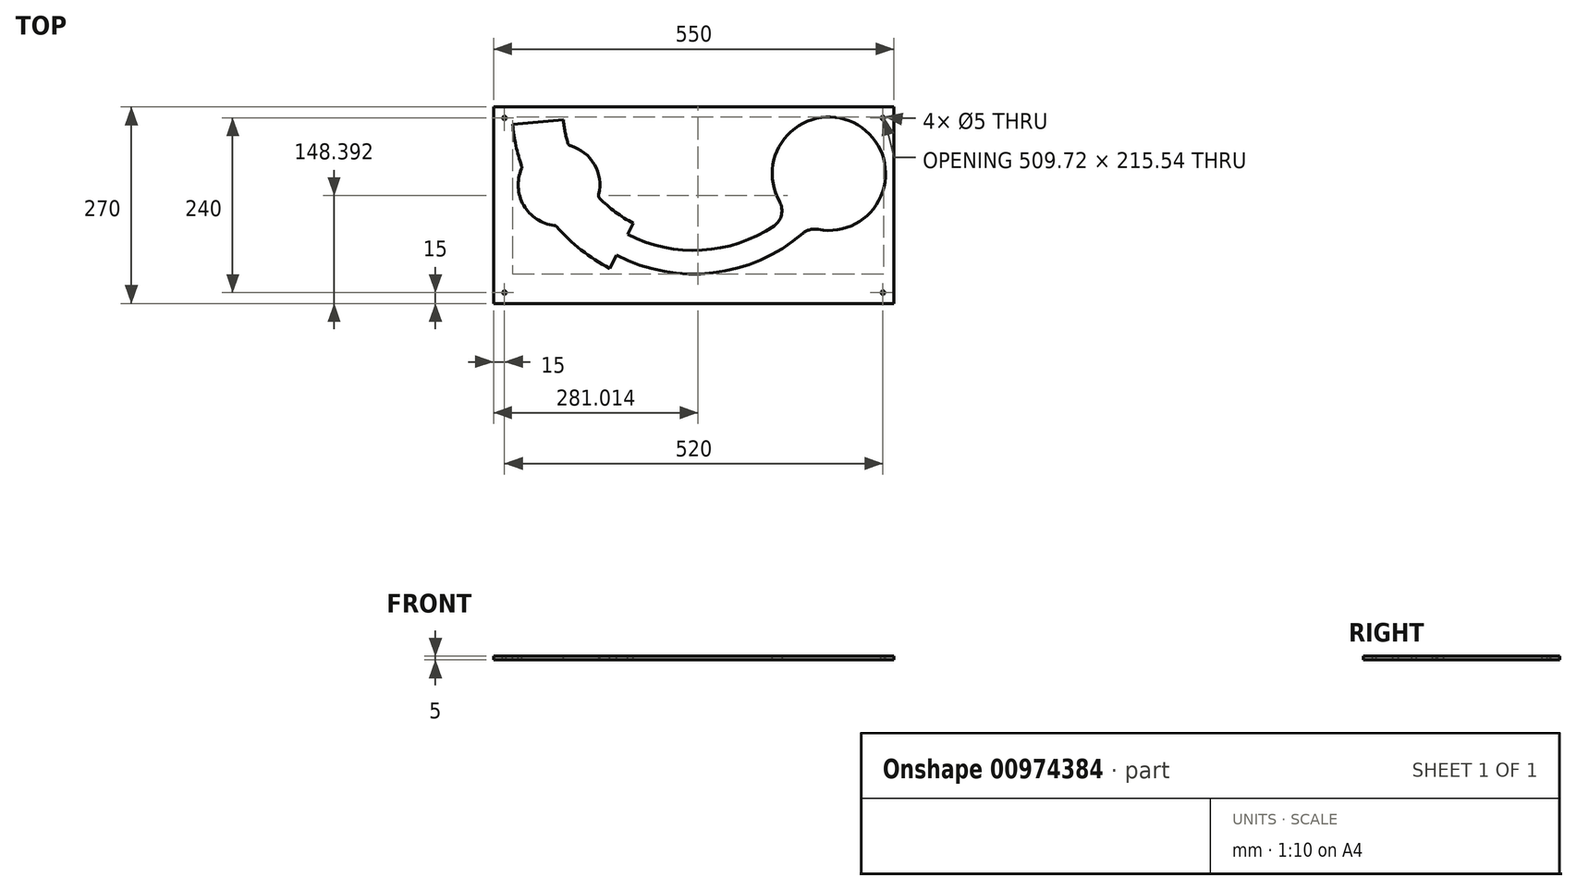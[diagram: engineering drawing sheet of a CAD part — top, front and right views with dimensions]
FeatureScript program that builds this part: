
annotation { "Feature Type Name" : "Feature", "Feature Type Description" : "" }
export const myFeature = defineFeature(function(context is Context, id is Id, definition is map)
    precondition{}
    {
        {
            var Q0;
            Q0=qCreatedBy(makeId("Top.planeOp"),FACE);
            var sketch = newSketch(context, id + "F0", { "sketchPlane" : qUnion([Q0])});
            skLineSegment(sketch, "E0.bottom", {"start": v(0, 0) * mm, "end": v(550, 0) * mm});
            skLineSegment(sketch, "E0.top", {"start": v(0, -270) * mm, "end": v(550, -270) * mm});
            skLineSegment(sketch, "E0.left", {"start": v(0, 0) * mm, "end": v(0, -270) * mm});
            skLineSegment(sketch, "E0.right", {"start": v(550, 0) * mm, "end": v(550, -270) * mm});
            skSolve(sketch);
        }
        {
            var Q0;
            Q0=makeQuery(id+"F0.imprint","IMPRINT",FACE,{"disambiguationData":[TD([[makeQuery(id+"F0.imprint","IMPRINT",EDGE,{"derivedFrom":sQuery(id+"F0.wireOp",EDGE,"E0.bottom")}),-1.0]])]});
            extrude(context, id + "F1", {"entities" : qUnion([Q0]), "oppositeDirection" : true, "depth" : 5 * mm, "offsetDistance" : 25 * mm});
        }
        {
            var Q0;
            Q0=makeQuery(id+"F1.opExtrude","CAP_FACE",FACE,{"disambiguationData":[OSD([sQuery(id+"F0.wireOp",EDGE,"E0.bottom"),sQuery(id+"F0.wireOp",EDGE,"E0.top"),sQuery(id+"F0.wireOp",EDGE,"E0.left"),sQuery(id+"F0.wireOp",EDGE,"E0.right")])],"isStart":true});
            var sketch = newSketch(context, id + "F2", { "sketchPlane" : qUnion([Q0])});
            skArc(sketch, "E1", {"start": v(26.15, -24) * mm, "mid": v(195.26, -236.94) * mm, "end": v(458.7, -169.57) * mm});
            skArc(sketch, "E2", {"start": v(95.83, -17.28) * mm, "mid": v(209.67, -167.73) * mm, "end": v(395.28, -133.91) * mm});
            skPoint(sketch, "E3.start.orphan", {"position": v(275, -180) * mm});
            skCircle(sketch, "E4", {"center": v(460.77, -91.66) * mm, "radius": 77.94 * mm});
            skLineSegment(sketch, "E5", {"start": v(95.83, -17.28) * mm, "end": v(26.15, -24) * mm});
            skLineSegment(sketch, "E6", {"start": v(191.91, -159.67) * mm, "end": v(159.6, -221.77) * mm});
            skLineSegment(sketch, "E7", {"start": v(550, 0) * mm, "end": v(535, 0) * mm});
            skLineSegment(sketch, "E8", {"start": v(535, 0) * mm, "end": v(535, -15) * mm});
            skLineSegment(sketch, "E9", {"start": v(0, -270) * mm, "end": v(15, -270) * mm});
            skLineSegment(sketch, "E10", {"start": v(15, -270) * mm, "end": v(15, -255) * mm});
            skCircle(sketch, "E11", {"center": v(15, -255) * mm, "radius": 2.5 * mm});
            skCircle(sketch, "E12", {"center": v(535, -255) * mm, "radius": 2.5 * mm});
            skCircle(sketch, "E13", {"center": v(535, -15) * mm, "radius": 2.5 * mm});
            skCircle(sketch, "E14", {"center": v(15, -15) * mm, "radius": 2.5 * mm});
            skCircle(sketch, "E15", {"center": v(89.9, -107.02) * mm, "radius": 56.06 * mm});
            skCircle(sketch, "E16", {"center": v(275, 0) * mm, "radius": 182 * mm});
            skCircle(sketch, "E17", {"center": v(275, 0) * mm, "radius": 239.5 * mm});
            skCircle(sketch, "E18", {"center": v(275, 0) * mm, "radius": 197 * mm});
            skCircle(sketch, "E19", {"center": v(275, 0) * mm, "radius": 229.5 * mm});
            skSolve(sketch);
        }
        {
            var Q0;
            {var subQ0=sQuery(id+"F2.wireOp",EDGE,"E4");var subQ1=makeQuery(id+"F2.imprint","INTERSECT",VERTEX,{"derivedFrom":[sQuery(id+"F2.wireOp",EDGE,"E1"),subQ0]});Q0=makeQuery(id+"F2.imprint","IMPRINT",FACE,{"disambiguationData":[TD([[makeQuery(id+"F2.imprint","IMPRINT",EDGE,{"disambiguationData":[TD([[subQ1,1.0]])],"derivedFrom":subQ0}),1.0]])]});}
            var Q1;
            {var subQ0=sQuery(id+"F2.wireOp",EDGE,"E19");var subQ1=sQuery(id+"F2.wireOp",EDGE,"E4");var subQ2=makeQuery(id+"F2.imprint","INTERSECT",VERTEX,{"disambiguationData":[OD(0.0)],"derivedFrom":[subQ1,subQ0]});Q1=makeQuery(id+"F2.imprint","IMPRINT",FACE,{"disambiguationData":[TD([[makeQuery(id+"F2.imprint","IMPRINT",EDGE,{"disambiguationData":[TD([[subQ2,1.0]])],"derivedFrom":subQ1}),1.0]])]});}
            var Q2;
            {var subQ0=sQuery(id+"F2.wireOp",EDGE,"E19");var subQ1=sQuery(id+"F2.wireOp",EDGE,"E4");var subQ2=makeQuery(id+"F2.imprint","INTERSECT",VERTEX,{"disambiguationData":[OD(0.0)],"derivedFrom":[subQ1,subQ0]});Q2=makeQuery(id+"F2.imprint","IMPRINT",FACE,{"disambiguationData":[TD([[makeQuery(id+"F2.imprint","IMPRINT",EDGE,{"disambiguationData":[TD([[subQ2,-1.0]])],"derivedFrom":subQ1}),1.0]])]});}
            var Q3;
            {var subQ0=sQuery(id+"F2.wireOp",EDGE,"E18");var subQ1=sQuery(id+"F2.wireOp",EDGE,"E4");var subQ2=makeQuery(id+"F2.imprint","INTERSECT",VERTEX,{"disambiguationData":[OD(0.0)],"derivedFrom":[subQ1,subQ0]});Q3=makeQuery(id+"F2.imprint","IMPRINT",FACE,{"disambiguationData":[TD([[makeQuery(id+"F2.imprint","IMPRINT",EDGE,{"disambiguationData":[TD([[subQ2,-1.0]])],"derivedFrom":subQ1}),1.0]])]});}
            var Q4;
            {var subQ0=sQuery(id+"F2.wireOp",EDGE,"E4");var subQ1=makeQuery(id+"F2.imprint","INTERSECT",VERTEX,{"derivedFrom":[sQuery(id+"F2.wireOp",EDGE,"E2"),subQ0]});Q4=makeQuery(id+"F2.imprint","IMPRINT",FACE,{"disambiguationData":[TD([[makeQuery(id+"F2.imprint","IMPRINT",EDGE,{"disambiguationData":[TD([[subQ1,1.0]])],"derivedFrom":subQ0}),1.0]])]});}
            var Q5;
            {var subQ0=sQuery(id+"F2.wireOp",EDGE,"E5");var subQ1=sQuery(id+"F2.wireOp",EDGE,"E1");var subQ2=makeQuery(id+"F2.imprint","INTERSECT",VERTEX,{"derivedFrom":[subQ1,subQ0]});Q5=makeQuery(id+"F2.imprint","IMPRINT",FACE,{"disambiguationData":[TD([[makeQuery(id+"F2.imprint","IMPRINT",EDGE,{"disambiguationData":[TD([[subQ2,-1.0]])],"derivedFrom":subQ1}),1.0]])]});}
            var Q6;
            {var subQ0=sQuery(id+"F2.wireOp",EDGE,"E19");var subQ1=sQuery(id+"F2.wireOp",EDGE,"E5");var subQ2=makeQuery(id+"F2.imprint","INTERSECT",VERTEX,{"derivedFrom":[subQ1,subQ0]});Q6=makeQuery(id+"F2.imprint","IMPRINT",FACE,{"disambiguationData":[TD([[makeQuery(id+"F2.imprint","IMPRINT",EDGE,{"disambiguationData":[TD([[subQ2,-1.0]])],"derivedFrom":subQ1}),1.0]])]});}
            var Q7;
            {var subQ0=sQuery(id+"F2.wireOp",EDGE,"E18");var subQ1=sQuery(id+"F2.wireOp",EDGE,"E5");var subQ2=makeQuery(id+"F2.imprint","INTERSECT",VERTEX,{"derivedFrom":[subQ1,subQ0]});Q7=makeQuery(id+"F2.imprint","IMPRINT",FACE,{"disambiguationData":[TD([[makeQuery(id+"F2.imprint","IMPRINT",EDGE,{"disambiguationData":[TD([[subQ2,-1.0]])],"derivedFrom":subQ1}),1.0]])]});}
            var Q8;
            {var subQ0=sQuery(id+"F2.wireOp",EDGE,"E16");var subQ1=sQuery(id+"F2.wireOp",EDGE,"E5");var subQ2=makeQuery(id+"F2.imprint","INTERSECT",VERTEX,{"derivedFrom":[subQ1,subQ0]});Q8=makeQuery(id+"F2.imprint","IMPRINT",FACE,{"disambiguationData":[TD([[makeQuery(id+"F2.imprint","IMPRINT",EDGE,{"disambiguationData":[TD([[subQ2,-1.0]])],"derivedFrom":subQ1}),1.0]])]});}
            var Q9;
            {var subQ0=sQuery(id+"F2.wireOp",EDGE,"E5");var subQ1=sQuery(id+"F2.wireOp",EDGE,"E2");var subQ2=makeQuery(id+"F2.imprint","INTERSECT",VERTEX,{"derivedFrom":[subQ1,subQ0]});Q9=makeQuery(id+"F2.imprint","IMPRINT",FACE,{"disambiguationData":[TD([[makeQuery(id+"F2.imprint","IMPRINT",EDGE,{"disambiguationData":[TD([[subQ2,-1.0]])],"derivedFrom":subQ1}),-1.0]])]});}
            var Q10;
            {var subQ0=sQuery(id+"F2.wireOp",EDGE,"E15");var subQ1=sQuery(id+"F2.wireOp",EDGE,"E2");var subQ2=makeQuery(id+"F2.imprint","INTERSECT",VERTEX,{"disambiguationData":[OD(0.0)],"derivedFrom":[subQ1,subQ0]});Q10=makeQuery(id+"F2.imprint","IMPRINT",FACE,{"disambiguationData":[TD([[makeQuery(id+"F2.imprint","IMPRINT",EDGE,{"disambiguationData":[TD([[subQ2,-1.0]])],"derivedFrom":subQ1}),1.0]])]});}
            var Q11;
            {var subQ0=sQuery(id+"F2.wireOp",EDGE,"E15");var subQ1=sQuery(id+"F2.wireOp",EDGE,"E2");var subQ2=makeQuery(id+"F2.imprint","INTERSECT",VERTEX,{"disambiguationData":[OD(0.0)],"derivedFrom":[subQ1,subQ0]});Q11=makeQuery(id+"F2.imprint","IMPRINT",FACE,{"disambiguationData":[TD([[makeQuery(id+"F2.imprint","IMPRINT",EDGE,{"disambiguationData":[TD([[subQ2,-1.0]])],"derivedFrom":subQ1}),-1.0]])]});}
            var Q12;
            {var subQ0=sQuery(id+"F2.wireOp",EDGE,"E16");var subQ1=sQuery(id+"F2.wireOp",EDGE,"E15");var subQ2=makeQuery(id+"F2.imprint","INTERSECT",VERTEX,{"disambiguationData":[OD(0.0)],"derivedFrom":[subQ1,subQ0]});Q12=makeQuery(id+"F2.imprint","IMPRINT",FACE,{"disambiguationData":[TD([[makeQuery(id+"F2.imprint","IMPRINT",EDGE,{"disambiguationData":[TD([[subQ2,-1.0]])],"derivedFrom":subQ1}),1.0]])]});}
            var Q13;
            {var subQ0=sQuery(id+"F2.wireOp",EDGE,"E18");var subQ1=sQuery(id+"F2.wireOp",EDGE,"E15");var subQ2=makeQuery(id+"F2.imprint","INTERSECT",VERTEX,{"disambiguationData":[OD(0.0)],"derivedFrom":[subQ1,subQ0]});Q13=makeQuery(id+"F2.imprint","IMPRINT",FACE,{"disambiguationData":[TD([[makeQuery(id+"F2.imprint","IMPRINT",EDGE,{"disambiguationData":[TD([[subQ2,-1.0]])],"derivedFrom":subQ1}),1.0]])]});}
            var Q14;
            {var subQ0=sQuery(id+"F2.wireOp",EDGE,"E19");var subQ1=sQuery(id+"F2.wireOp",EDGE,"E15");var subQ2=makeQuery(id+"F2.imprint","INTERSECT",VERTEX,{"disambiguationData":[OD(0.0)],"derivedFrom":[subQ1,subQ0]});Q14=makeQuery(id+"F2.imprint","IMPRINT",FACE,{"disambiguationData":[TD([[makeQuery(id+"F2.imprint","IMPRINT",EDGE,{"disambiguationData":[TD([[subQ2,-1.0]])],"derivedFrom":subQ1}),1.0]])]});}
            var Q15;
            {var subQ0=sQuery(id+"F2.wireOp",EDGE,"E15");var subQ1=sQuery(id+"F2.wireOp",EDGE,"E1");var subQ2=makeQuery(id+"F2.imprint","INTERSECT",VERTEX,{"disambiguationData":[OD(0.0)],"derivedFrom":[subQ1,subQ0]});Q15=makeQuery(id+"F2.imprint","IMPRINT",FACE,{"disambiguationData":[TD([[makeQuery(id+"F2.imprint","IMPRINT",EDGE,{"disambiguationData":[TD([[subQ2,-1.0]])],"derivedFrom":subQ1}),1.0]])]});}
            var Q16;
            {var subQ0=sQuery(id+"F2.wireOp",EDGE,"E15");var subQ1=sQuery(id+"F2.wireOp",EDGE,"E1");var subQ2=makeQuery(id+"F2.imprint","INTERSECT",VERTEX,{"disambiguationData":[OD(0.0)],"derivedFrom":[subQ1,subQ0]});Q16=makeQuery(id+"F2.imprint","IMPRINT",FACE,{"disambiguationData":[TD([[makeQuery(id+"F2.imprint","IMPRINT",EDGE,{"disambiguationData":[TD([[subQ2,-1.0]])],"derivedFrom":subQ1}),-1.0]])]});}
            var Q17;
            {var subQ0=sQuery(id+"F2.wireOp",EDGE,"E6");var subQ1=sQuery(id+"F2.wireOp",EDGE,"E2");var subQ2=makeQuery(id+"F2.imprint","INTERSECT",VERTEX,{"derivedFrom":[subQ1,subQ0]});Q17=makeQuery(id+"F2.imprint","IMPRINT",FACE,{"disambiguationData":[TD([[makeQuery(id+"F2.imprint","IMPRINT",EDGE,{"disambiguationData":[TD([[subQ2,1.0]])],"derivedFrom":subQ1}),-1.0]])]});}
            var Q18;
            {var subQ0=sQuery(id+"F2.wireOp",EDGE,"E16");var subQ1=sQuery(id+"F2.wireOp",EDGE,"E6");var subQ2=makeQuery(id+"F2.imprint","INTERSECT",VERTEX,{"derivedFrom":[subQ1,subQ0]});Q18=makeQuery(id+"F2.imprint","IMPRINT",FACE,{"disambiguationData":[TD([[makeQuery(id+"F2.imprint","IMPRINT",EDGE,{"disambiguationData":[TD([[subQ2,-1.0]])],"derivedFrom":subQ1}),-1.0]])]});}
            var Q19;
            {var subQ0=sQuery(id+"F2.wireOp",EDGE,"E18");var subQ1=sQuery(id+"F2.wireOp",EDGE,"E6");var subQ2=makeQuery(id+"F2.imprint","INTERSECT",VERTEX,{"derivedFrom":[subQ1,subQ0]});Q19=makeQuery(id+"F2.imprint","IMPRINT",FACE,{"disambiguationData":[TD([[makeQuery(id+"F2.imprint","IMPRINT",EDGE,{"disambiguationData":[TD([[subQ2,-1.0]])],"derivedFrom":subQ1}),-1.0]])]});}
            var Q20;
            {var subQ0=sQuery(id+"F2.wireOp",EDGE,"E19");var subQ1=sQuery(id+"F2.wireOp",EDGE,"E6");var subQ2=makeQuery(id+"F2.imprint","INTERSECT",VERTEX,{"derivedFrom":[subQ1,subQ0]});Q20=makeQuery(id+"F2.imprint","IMPRINT",FACE,{"disambiguationData":[TD([[makeQuery(id+"F2.imprint","IMPRINT",EDGE,{"disambiguationData":[TD([[subQ2,-1.0]])],"derivedFrom":subQ1}),-1.0]])]});}
            var Q21;
            {var subQ0=sQuery(id+"F2.wireOp",EDGE,"E6");var subQ1=sQuery(id+"F2.wireOp",EDGE,"E1");var subQ2=makeQuery(id+"F2.imprint","INTERSECT",VERTEX,{"derivedFrom":[subQ1,subQ0]});Q21=makeQuery(id+"F2.imprint","IMPRINT",FACE,{"disambiguationData":[TD([[makeQuery(id+"F2.imprint","IMPRINT",EDGE,{"disambiguationData":[TD([[subQ2,1.0]])],"derivedFrom":subQ1}),1.0]])]});}
            var Q22;
            {var subQ0=sQuery(id+"F2.wireOp",EDGE,"E18");var subQ1=sQuery(id+"F2.wireOp",EDGE,"E4");var subQ2=makeQuery(id+"F2.imprint","INTERSECT",VERTEX,{"disambiguationData":[OD(1.0)],"derivedFrom":[subQ1,subQ0]});Q22=makeQuery(id+"F2.imprint","IMPRINT",FACE,{"disambiguationData":[TD([[makeQuery(id+"F2.imprint","IMPRINT",EDGE,{"disambiguationData":[TD([[subQ2,-1.0]])],"derivedFrom":subQ1}),-1.0]])]});}
            extrude(context, id + "F3", {"entities" : qUnion([Q0, Q1, Q2, Q3, Q4, Q5, Q6, Q7, Q8, Q9, Q10, Q11, Q12, Q13, Q14, Q15, Q16, Q17, Q18, Q19, Q20, Q21, Q22]), "operationType" : NewBodyOperationType.REMOVE, "oppositeDirection" : true, "depth" : 25 * mm, "offsetDistance" : 25 * mm});
        }
        {
            var Q0;
            Q0=makeQuery(id+"F3.boolean.opBoolean","COPY",EDGE,{"derivedFrom":makeQuery(id+"F3.opExtrude","SWEPT_EDGE",EDGE,{"disambiguationData":[OSD([sQuery(id+"F2.wireOp",EDGE,"E4"),sQuery(id+"F2.wireOp",EDGE,"E18")])]})});
            var Q1;
            Q1=makeQuery(id+"F3.boolean.opBoolean","COPY",EDGE,{"derivedFrom":makeQuery(id+"F3.opExtrude","SWEPT_EDGE",EDGE,{"disambiguationData":[OSD([sQuery(id+"F2.wireOp",EDGE,"E4"),sQuery(id+"F2.wireOp",EDGE,"E19")])]})});
            fillet(context, id + "F4", {"entities" : qUnion([Q0, Q1]), "radius" : 25 * mm, "tangentPropagation" : true, "allowEdgeOverflow" : false});
        }
        {
            var Q0;
            Q0=makeQuery(id+"F2.imprint","IMPRINT",FACE,{"disambiguationData":[TD([[makeQuery(id+"F2.imprint","IMPRINT",EDGE,{"derivedFrom":sQuery(id+"F2.wireOp",EDGE,"E14")}),1.0]])]});
            var Q1;
            Q1=makeQuery(id+"F2.imprint","IMPRINT",FACE,{"disambiguationData":[TD([[makeQuery(id+"F2.imprint","IMPRINT",EDGE,{"derivedFrom":sQuery(id+"F2.wireOp",EDGE,"E11")}),1.0]])]});
            var Q2;
            Q2=makeQuery(id+"F2.imprint","IMPRINT",FACE,{"disambiguationData":[TD([[makeQuery(id+"F2.imprint","IMPRINT",EDGE,{"derivedFrom":sQuery(id+"F2.wireOp",EDGE,"E12")}),1.0]])]});
            var Q3;
            Q3=makeQuery(id+"F2.imprint","IMPRINT",FACE,{"disambiguationData":[TD([[makeQuery(id+"F2.imprint","IMPRINT",EDGE,{"derivedFrom":sQuery(id+"F2.wireOp",EDGE,"E13")}),1.0]])]});
            extrude(context, id + "F5", {"entities" : qUnion([Q0, Q1, Q2, Q3]), "operationType" : NewBodyOperationType.REMOVE, "oppositeDirection" : true, "depth" : 25 * mm, "offsetDistance" : 25 * mm});
        }
        {
            var Q0;
            {var subQ0=sQuery(id+"F2.wireOp",EDGE,"E15");var subQ1=sQuery(id+"F2.wireOp",EDGE,"E2");Q0=makeQuery(id+"F3.boolean.opBoolean","COPY",EDGE,{"derivedFrom":makeQuery(id+"F3.opExtrude","SWEPT_EDGE",EDGE,{"disambiguationData":[OSD([subQ1,subQ0]),TDD([makeQuery(id+"F2.imprint","INTERSECT",VERTEX,{"disambiguationData":[OD(0.0)],"derivedFrom":[subQ1,subQ0]})])]})});}
            var Q1;
            {var subQ0=sQuery(id+"F2.wireOp",EDGE,"E15");var subQ1=sQuery(id+"F2.wireOp",EDGE,"E2");Q1=makeQuery(id+"F3.boolean.opBoolean","COPY",EDGE,{"derivedFrom":makeQuery(id+"F3.opExtrude","SWEPT_EDGE",EDGE,{"disambiguationData":[OSD([subQ1,subQ0]),TDD([makeQuery(id+"F2.imprint","INTERSECT",VERTEX,{"disambiguationData":[OD(1.0)],"derivedFrom":[subQ1,subQ0]})])]})});}
            var Q2;
            {var subQ0=sQuery(id+"F2.wireOp",EDGE,"E15");var subQ1=sQuery(id+"F2.wireOp",EDGE,"E1");Q2=makeQuery(id+"F3.boolean.opBoolean","COPY",EDGE,{"derivedFrom":makeQuery(id+"F3.opExtrude","SWEPT_EDGE",EDGE,{"disambiguationData":[OSD([subQ1,subQ0]),TDD([makeQuery(id+"F2.imprint","INTERSECT",VERTEX,{"disambiguationData":[OD(0.0)],"derivedFrom":[subQ1,subQ0]})])]})});}
            var Q3;
            {var subQ0=sQuery(id+"F2.wireOp",EDGE,"E15");var subQ1=sQuery(id+"F2.wireOp",EDGE,"E1");Q3=makeQuery(id+"F3.boolean.opBoolean","COPY",EDGE,{"derivedFrom":makeQuery(id+"F3.opExtrude","SWEPT_EDGE",EDGE,{"disambiguationData":[OSD([subQ1,subQ0]),TDD([makeQuery(id+"F2.imprint","INTERSECT",VERTEX,{"disambiguationData":[OD(1.0)],"derivedFrom":[subQ1,subQ0]})])]})});}
            fillet(context, id + "F6", {"entities" : qUnion([Q0, Q1, Q2, Q3]), "radius" : 5 * mm, "tangentPropagation" : true, "allowEdgeOverflow" : false});
        }
    });
